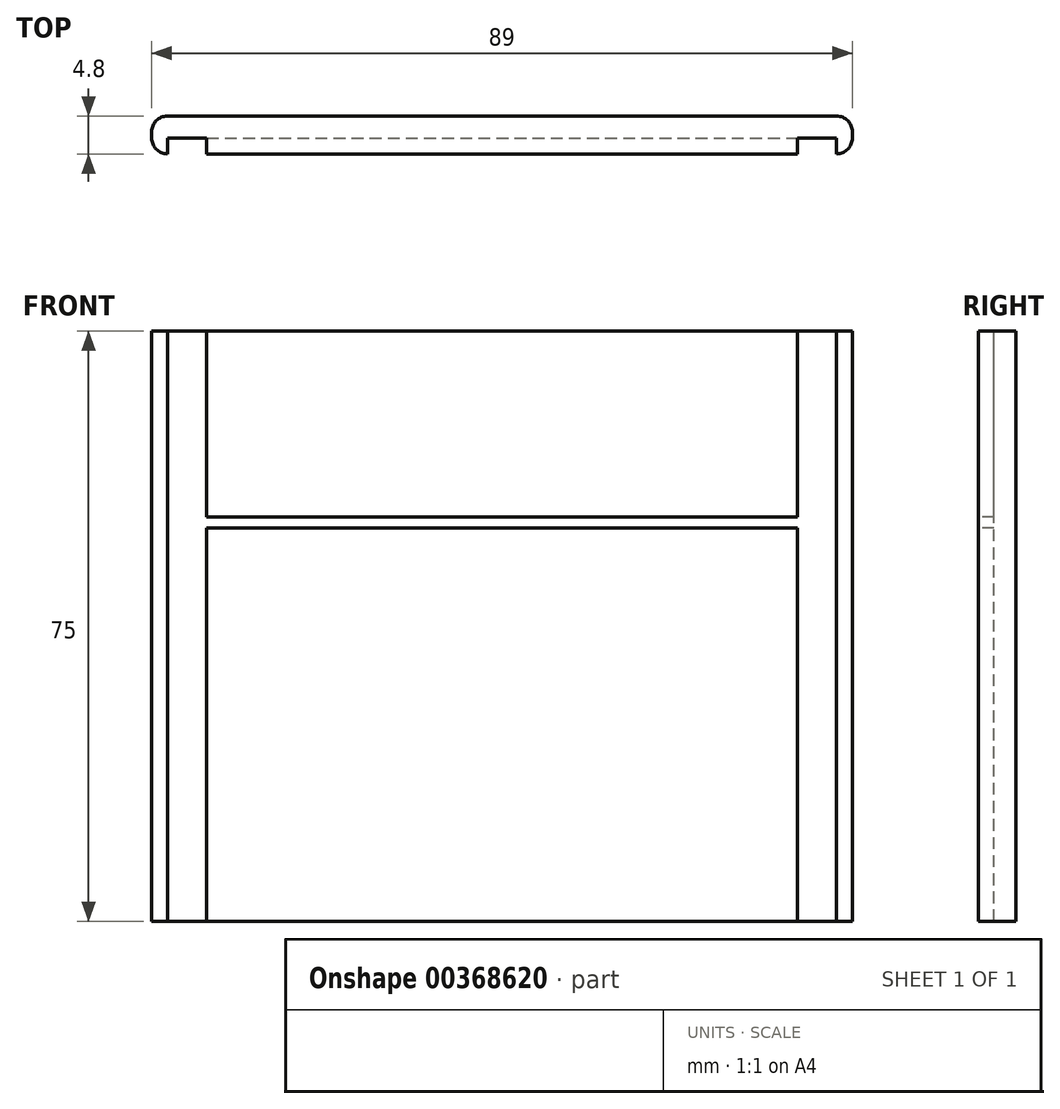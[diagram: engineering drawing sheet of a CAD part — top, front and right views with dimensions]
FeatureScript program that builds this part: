
annotation { "Feature Type Name" : "Feature", "Feature Type Description" : "" }
export const myFeature = defineFeature(function(context is Context, id is Id, definition is map)
    precondition{}
    {
        {
            var Q0;
            Q0=qCreatedBy(makeId("Front.planeOp"),FACE);
            var sketch = newSketch(context, id + "F0", { "sketchPlane" : qUnion([Q0])});
            skLineSegment(sketch, "E0.bottom", {"start": v(44.5, -37.5) * mm, "end": v(-44.5, -37.5) * mm});
            skLineSegment(sketch, "E0.top", {"start": v(44.5, 37.5) * mm, "end": v(-44.5, 37.5) * mm});
            skLineSegment(sketch, "E0.left", {"start": v(44.5, -37.5) * mm, "end": v(44.5, 37.5) * mm});
            skLineSegment(sketch, "E0.right", {"start": v(-44.5, -37.5) * mm, "end": v(-44.5, 37.5) * mm});
            skPoint(sketch, "E0.middle", {"position": v(0, 0) * mm});
            skSolve(sketch);
        }
        {
            var Q0;
            Q0=qSketchRegion(id+"F0",true);
            extrude(context, id + "F1", {"entities" : qUnion([Q0]), "depth" : 4.8 * mm});
        }
        {
            var Q0;
            Q0=makeQuery(id+"F1.opExtrude","CAP_FACE",FACE,{"disambiguationData":[OSD([sQuery(id+"F0.wireOp",EDGE,"E0.bottom"),sQuery(id+"F0.wireOp",EDGE,"E0.top"),sQuery(id+"F0.wireOp",EDGE,"E0.left"),sQuery(id+"F0.wireOp",EDGE,"E0.right")])],"isStart":false});
            var sketch = newSketch(context, id + "F2", { "sketchPlane" : qUnion([Q0])});
            skPoint(sketch, "E1.middle", {"position": v(0, 13.2) * mm});
            skLineSegment(sketch, "E2.bottom", {"start": v(-42.5, -37.5) * mm, "end": v(-37.5, -37.5) * mm});
            skLineSegment(sketch, "E2.top", {"start": v(-42.5, 37.5) * mm, "end": v(-37.5, 37.5) * mm});
            skLineSegment(sketch, "E2.left", {"start": v(-42.5, -37.5) * mm, "end": v(-42.5, 37.5) * mm});
            skLineSegment(sketch, "E2.right", {"start": v(-37.5, -37.5) * mm, "end": v(-37.5, 37.5) * mm});
            skPoint(sketch, "E2.middle", {"position": v(-40, 0) * mm});
            skLineSegment(sketch, "E3.bottom", {"start": v(37.5, -37.5) * mm, "end": v(42.5, -37.5) * mm});
            skLineSegment(sketch, "E3.top", {"start": v(37.5, 37.5) * mm, "end": v(42.5, 37.5) * mm});
            skLineSegment(sketch, "E3.left", {"start": v(37.5, -37.5) * mm, "end": v(37.5, 37.5) * mm});
            skLineSegment(sketch, "E3.right", {"start": v(42.5, -37.5) * mm, "end": v(42.5, 37.5) * mm});
            skPoint(sketch, "E3.middle", {"position": v(40, 0) * mm});
            skPoint(sketch, "E3.middle.positionSnap0", {"position": v(-37.5, 0) * mm});
            skPoint(sketch, "E3.centerSnap0", {"position": v(-37.5, 0) * mm});
            skLineSegment(sketch, "E4.bottom", {"start": v(-37.5, 12.5) * mm, "end": v(37.5, 12.5) * mm});
            skLineSegment(sketch, "E4.top", {"start": v(-37.5, 13.9) * mm, "end": v(37.5, 13.9) * mm});
            skLineSegment(sketch, "E4.left", {"start": v(-37.5, 12.5) * mm, "end": v(-37.5, 13.9) * mm});
            skLineSegment(sketch, "E4.right", {"start": v(37.5, 12.5) * mm, "end": v(37.5, 13.9) * mm});
            skSolve(sketch);
        }
        {
            var Q0;
            Q0=qSketchRegion(id+"F2",true);
            extrude(context, id + "F3", {"entities" : qUnion([Q0]), "operationType" : NewBodyOperationType.REMOVE, "oppositeDirection" : true, "depth" : 2 * mm});
        }
        {
            var Q0;
            {var subQ0=sQuery(id+"F0.wireOp",EDGE,"E0.right");var subQ1=sQuery(id+"F0.wireOp",EDGE,"E0.top");var subQ3=makeQuery(id+"F1.opExtrude","CAP_EDGE",EDGE,{"disambiguationData":[OSD([subQ0])],"isStart":false});Q0=makeQuery(id+"F3.boolean.opBoolean","SPLIT",EDGE,{"disambiguationData":[TD([makeQuery(id+"F1.opExtrude","SWEPT_FACE",FACE,{"disambiguationData":[OSD([subQ1])]})])],"derivedFrom":subQ3});}
            var Q1;
            {var subQ0=sQuery(id+"F0.wireOp",EDGE,"E0.bottom");var subQ1=sQuery(id+"F0.wireOp",EDGE,"E0.right");var subQ3=makeQuery(id+"F1.opExtrude","CAP_EDGE",EDGE,{"disambiguationData":[OSD([subQ1])],"isStart":false});Q1=makeQuery(id+"F3.boolean.opBoolean","SPLIT",EDGE,{"disambiguationData":[TD([makeQuery(id+"F1.opExtrude","SWEPT_FACE",FACE,{"disambiguationData":[OSD([subQ0])]})])],"derivedFrom":subQ3});}
            var Q2;
            {var subQ0=sQuery(id+"F0.wireOp",EDGE,"E0.left");var subQ1=sQuery(id+"F0.wireOp",EDGE,"E0.top");var subQ3=makeQuery(id+"F1.opExtrude","CAP_EDGE",EDGE,{"disambiguationData":[OSD([subQ0])],"isStart":false});Q2=makeQuery(id+"F3.boolean.opBoolean","SPLIT",EDGE,{"disambiguationData":[TD([makeQuery(id+"F1.opExtrude","SWEPT_FACE",FACE,{"disambiguationData":[OSD([subQ1])]})])],"derivedFrom":subQ3});}
            var Q3;
            {var subQ0=sQuery(id+"F0.wireOp",EDGE,"E0.bottom");var subQ1=sQuery(id+"F0.wireOp",EDGE,"E0.left");var subQ3=makeQuery(id+"F1.opExtrude","CAP_EDGE",EDGE,{"disambiguationData":[OSD([subQ1])],"isStart":false});Q3=makeQuery(id+"F3.boolean.opBoolean","SPLIT",EDGE,{"disambiguationData":[TD([makeQuery(id+"F1.opExtrude","SWEPT_FACE",FACE,{"disambiguationData":[OSD([subQ0])]})])],"derivedFrom":subQ3});}
            var Q4;
            Q4=makeQuery(id+"F1.opExtrude","CAP_EDGE",EDGE,{"disambiguationData":[OSD([sQuery(id+"F0.wireOp",EDGE,"E0.left")])],"isStart":true});
            var Q5;
            Q5=makeQuery(id+"F1.opExtrude","CAP_EDGE",EDGE,{"disambiguationData":[OSD([sQuery(id+"F0.wireOp",EDGE,"E0.right")])],"isStart":true});
            fillet(context, id + "F4", {"entities" : qUnion([Q0, Q1, Q2, Q3, Q4, Q5]), "radius" : 2 * mm, "tangentPropagation" : true, "allowEdgeOverflow" : false});
        }
    });
